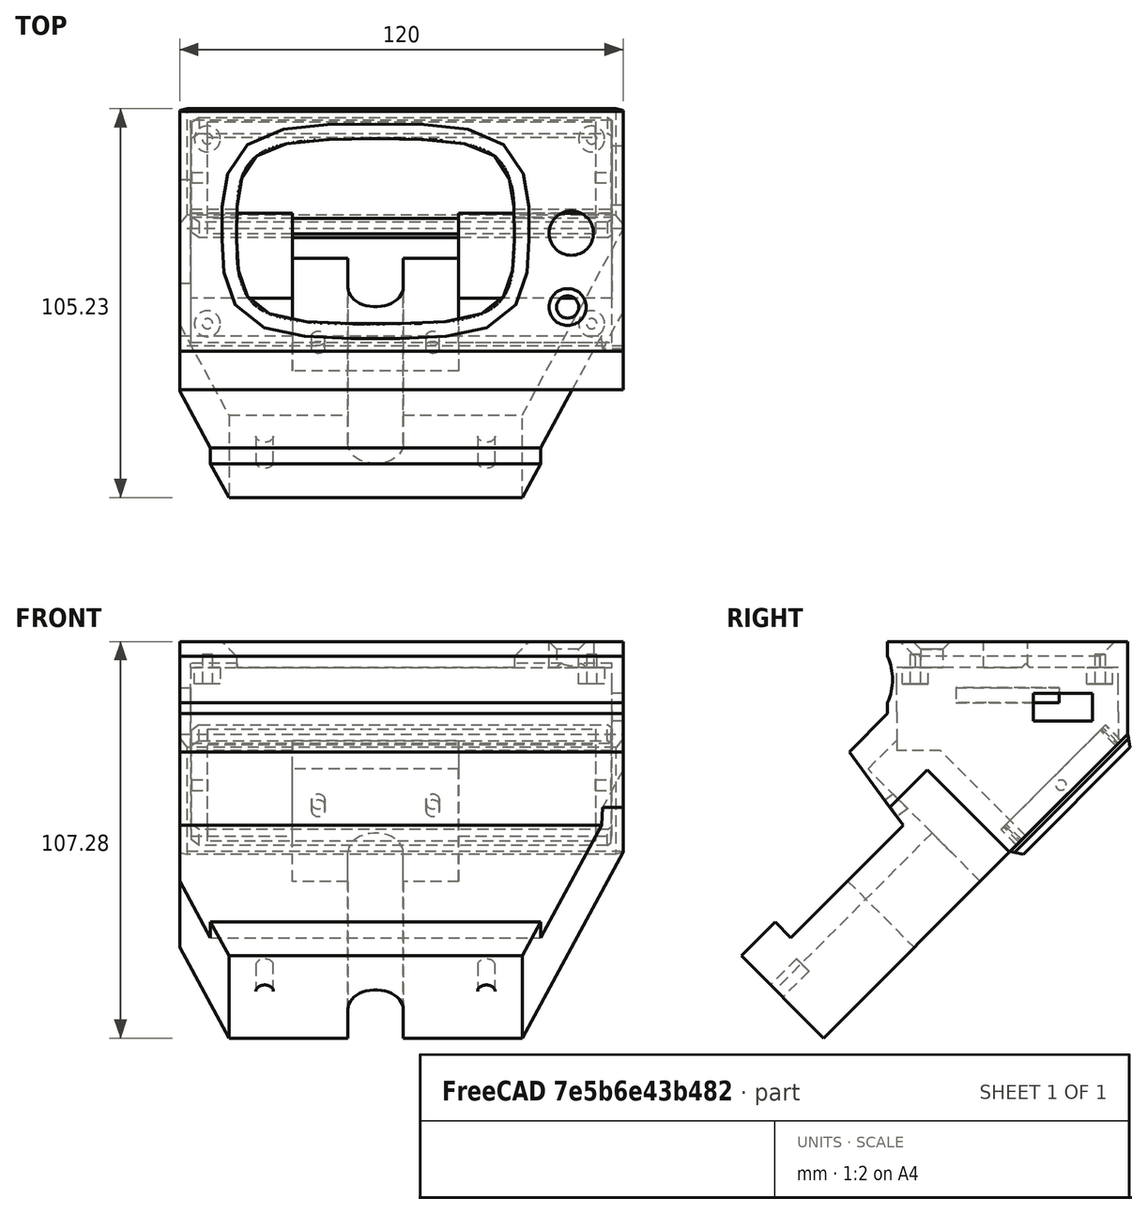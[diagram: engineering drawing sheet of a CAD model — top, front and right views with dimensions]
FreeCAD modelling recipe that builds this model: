
FCSTD DOCUMENT  (FreeCAD 0.19R)
Label: ScreenBezel2
License: All rights reserved
LicenseURL: http://en.wikipedia.org/wiki/All_rights_reserved
objects: Sketcher::SketchObject×24, PartDesign::Pocket×19, PartDesign::Chamfer×7, PartDesign::Pad×5, PartDesign::Body×2, PartDesign::Mirrored×1, Mesh::Feature×1
note: 89 computed .brp shape members not serialized (recipe doc carries the construction recipe); baked Part::Feature solids carry a one-line shape summary decoded from their .brp

FEATURE [Sketcher::SketchObject] Sketch
  FullyConstrained = true
  MapMode = 5
  Support = -> [XY_Plane]
  sketch-geometry (30):
    g0: LineSegment StartX=-53 StartY=32.5 StartZ=0 EndX=67 EndY=32.5 EndZ=0
    g1: LineSegment StartX=67 StartY=32.5 StartZ=0 EndX=67 EndY=-32.5 EndZ=0
    g2: LineSegment StartX=67 StartY=-32.5 StartZ=0 EndX=-53 EndY=-32.5 EndZ=0
    g3: LineSegment StartX=-53 StartY=-32.5 StartZ=0 EndX=-53 EndY=32.5 EndZ=0
    g4: LineSegment StartX=-37 StartY=24.5 StartZ=0 EndX=37 EndY=24.5 EndZ=0
    g5: LineSegment StartX=37 StartY=24.5 StartZ=0 EndX=37 EndY=-24.5 EndZ=0
    g6: LineSegment StartX=37 StartY=-24.5 StartZ=0 EndX=-37 EndY=-24.5 EndZ=0
    g7: LineSegment StartX=-37 StartY=-24.5 StartZ=0 EndX=-37 EndY=24.5 EndZ=0
    g8: LineSegment StartX=-37.7408 StartY=25.116 StartZ=0 EndX=37.7408 EndY=25.116 EndZ=0
    g9: LineSegment StartX=37.7408 StartY=25.116 StartZ=0 EndX=37.7408 EndY=-25.116 EndZ=0
    g10: LineSegment StartX=37.7408 StartY=-25.116 StartZ=0 EndX=-37.7408 EndY=-25.116 EndZ=0
    g11: LineSegment StartX=-37.7408 StartY=-25.116 StartZ=0 EndX=-37.7408 EndY=25.116 EndZ=0
    g12-g19: Circle x8 (B-spline internal-alignment scaffolding for g20; pole/knot coordinates omitted)
    g20: BSplineCurve PolesCount=8 KnotsCount=9 Degree=3 IsPeriodic=1
    g21-g29: GeomPoint x9 (B-spline internal-alignment scaffolding for g20; pole/knot coordinates omitted)
  constraints (53):
    c: Coincident(g0,g1)
    c: Coincident(g1,g2)
    c: Coincident(g2,g3)
    c: Coincident(g3,g0)
    c: Horizontal(g0)
    c: Horizontal(g2)
    c: Vertical(g1)
    c: Vertical(g3)
    c: Coincident(g4,g5)
    c: Coincident(g5,g6)
    c: Coincident(g6,g7)
    c: Coincident(g7,g4)
    c: Horizontal(g4)
    c: Vertical(g7)
    c: Distance(g5) = 49
    c: Distance(g4,g3) = 16
    c: Distance(g0,g5) = 30
    c: Distance(g6,g2) = 8
    c: Distance(g4,g0) = 8
    c: Distance(g6) = 74
    c: Symmetric(g5,g6,g-2)
    c: Symmetric(g5,g4,g-1)
    c: Coincident(g8,g9)
    c: Coincident(g9,g10)
    c: Coincident(g10,g11)
    c: Coincident(g11,g8)
    c: Horizontal(g8)
    c: Horizontal(g10)
    c: Vertical(g9)
    c: Vertical(g11)
    c: Symmetric(g9,g8,g-1)
    c: Weight(g12) = 1
    c: Equal(g12,g13)
    c: Equal(g12,g14)
    c: Equal(g12,g15)
    c: PointOnObject(g15,g-1)
    c: Equal(g12,g16)
    c: Equal(g12,g17)
    c: PointOnObject(g17,g-2)
    c: Equal(g12,g18)
    c: Equal(g12,g19)
    c: InternalAlignment(g12-g19 -> g20) x8
    c: InternalAlignment(g21-g29 -> g20) x9
    c: Coincident(g8,g12)
    c: Coincident(g14,g8)
    c: Coincident(g16,g10)
    c: Coincident(g18,g9)
    c: Distance(g19,g5) = 0.5
    c: Symmetric(g19,g15,g-2)
    c: Distance(g17,g6) = 0.5
    c: Symmetric(g17,g13,g-1)
    c: DistanceX(g8) = 37.7408
    c: DistanceY(g8) = 25.116
FEATURE [PartDesign::Pad] Pad
  Direction = (1,1,1)
  Length = 25
  Length2 = 100
  Profile = -> Sketch
  Type = 0
FEATURE [Sketcher::SketchObject] Sketch004  label="knob"
  FullyConstrained = false
  MapMode = 5
  Placement = pos=(0,0,0) rot=(1,0,0;3.14159rad)
  sketch-geometry (1):
    g0: Circle CenterX=52 CenterY=20.5 CenterZ=0 NormalX=0 NormalY=0 NormalZ=1 AngleXU=0 Radius=3
  constraints (1):
    c: Diameter(g0) = 6
FEATURE [PartDesign::Pocket] Pocket001
  BaseFeature = -> Pad
  Length = 5
  Length2 = 100
  Profile = -> Sketch004
  Type = 1
FEATURE [Sketcher::SketchObject] Sketch001  label="knob001"
  FullyConstrained = false
  MapMode = 5
  Placement = pos=(0,0,25) rot=(0,0,1;0rad)
  Support = -> [Pocket001]
  sketch-geometry (1):
    g0: Circle CenterX=53 CenterY=-0.5 CenterZ=0 NormalX=0 NormalY=0 NormalZ=1 AngleXU=0 Radius=6
  constraints (2):
    c: Diameter(g0) = 12
    c: DistanceY(g0) = -0.5
FEATURE [PartDesign::Pocket] Pocket
  BaseFeature = -> Pocket001
  Length = 5
  Length2 = 100
  Profile = -> Sketch001
  Type = 1
FEATURE [Sketcher::SketchObject] Sketch005  label="MainPCBPocket"
  FullyConstrained = true
  MapMode = 5
  Placement = pos=(0,0,0) rot=(1,0,0;3.14159rad)
  Support = -> [Pocket]
  sketch-geometry (4):
    g0: LineSegment StartX=-50 StartY=30 StartZ=0 EndX=64 EndY=30 EndZ=0
    g1: LineSegment StartX=64 StartY=30 StartZ=0 EndX=64 EndY=-30 EndZ=0
    g2: LineSegment StartX=64 StartY=-30 StartZ=0 EndX=-50 EndY=-30 EndZ=0
    g3: LineSegment StartX=-50 StartY=-30 StartZ=0 EndX=-50 EndY=30 EndZ=0
  constraints (11):
    c: Coincident(g0,g1)
    c: Coincident(g1,g2)
    c: Coincident(g2,g3)
    c: Coincident(g3,g0)
    c: Horizontal(g0)
    c: Horizontal(g2)
    c: Vertical(g1)
    c: Symmetric(g2,g0,g-1)
    c: DistanceX(g0) = -50
    c: DistanceY(g0) = 30
    c: DistanceX(g1) = 64
FEATURE [PartDesign::Pocket] Pocket002
  BaseFeature = -> Pocket
  Length = 18
  Length2 = 100
  Profile = -> Sketch005
  Type = 0
FEATURE [PartDesign::Chamfer] Chamfer
  Angle = 45
  Base = -> Pocket002 [Edge19]
  BaseFeature = -> Pocket002
  ChamferType = 0
  FlipDirection = false
  Size = 4
  Size2 = 1
  SupportTransform = false
FEATURE [Sketcher::SketchObject] Sketch006  label="standofs"
  FullyConstrained = true
  MapMode = 5
  Placement = pos=(0,0,18) rot=(1,0,0;3.14159rad)
  Support = -> [Chamfer]
  sketch-geometry (4):
    g0: Circle CenterX=-45.5 CenterY=25 CenterZ=0 NormalX=0 NormalY=0 NormalZ=1 AngleXU=0 Radius=3.5
    g1: Circle CenterX=-45.5 CenterY=-25 CenterZ=0 NormalX=0 NormalY=0 NormalZ=1 AngleXU=0 Radius=3.5
    g2: Circle CenterX=58.5 CenterY=-25 CenterZ=0 NormalX=0 NormalY=0 NormalZ=1 AngleXU=0 Radius=3.5
    g3: Circle CenterX=58.5 CenterY=25 CenterZ=0 NormalX=0 NormalY=0 NormalZ=1 AngleXU=0 Radius=3.5
  constraints (10):
    c: Diameter(g0) = 7
    c: Equal(g0,g1)
    c: Equal(g0,g3)
    c: Equal(g0,g2)
    c: Symmetric(g1,g0,g-1)
    c: Symmetric(g2,g3,g-1)
    c: Distance(g3,g2) = 50
    c: Distance(g1,g0) = 50
    c: Distance(g3,g0) = 104
    c: DistanceX(g0) = -45.5
FEATURE [PartDesign::Pad] Pad001
  BaseFeature = -> Chamfer
  Direction = (1,1,1)
  Length = 4.5
  Length2 = 100
  Profile = -> Sketch006
  Type = 0
FEATURE [Sketcher::SketchObject] Sketch007  label="holes"
  FullyConstrained = true
  MapMode = 5
  Placement = pos=(0,0,13.5) rot=(1,0,0;3.14159rad)
  Support = -> [Pad001]
  sketch-geometry (4):
    g0: Circle CenterX=-45.5 CenterY=25 CenterZ=0 NormalX=0 NormalY=0 NormalZ=1 AngleXU=0 Radius=1.4
    g1: Circle CenterX=58.5 CenterY=25 CenterZ=0 NormalX=0 NormalY=0 NormalZ=1 AngleXU=0 Radius=1.4
    g2: Circle CenterX=58.5 CenterY=-25 CenterZ=0 NormalX=0 NormalY=0 NormalZ=1 AngleXU=0 Radius=1.4
    g3: Circle CenterX=-45.5 CenterY=-25 CenterZ=0 NormalX=0 NormalY=0 NormalZ=1 AngleXU=0 Radius=1.4
  constraints (10):
    c: Distance(g3,g2) = 104
    c: Distance(g3,g0) = 50
    c: Symmetric(g3,g0,g-1)
    c: Symmetric(g2,g1,g-1)
    c: Diameter(g1) = 2.8
    c: Equal(g1,g2)
    c: Equal(g1,g3)
    c: Equal(g1,g0)
    c: DistanceX(g0) = -45.5
    c: Distance(g1,g2) = 50
FEATURE [PartDesign::Pocket] Pocket003
  BaseFeature = -> Pad001
  Length = 8
  Length2 = 100
  Profile = -> Sketch007
  Type = 0
FEATURE [Sketcher::SketchObject] Sketch008  label="USBhole"
  ExternalGeometry = -> [Pocket003]
  FullyConstrained = true
  MapMode = 5
  Placement = pos=(67,0,0) rot=(0.57735,0.57735,0.57735;2.0944rad)
  Support = -> [Pocket003]
  sketch-geometry (4):
    g0: LineSegment StartX=7 StartY=6.5 StartZ=0 EndX=23 EndY=6.5 EndZ=0
    g1: LineSegment StartX=23 StartY=6.5 StartZ=0 EndX=23 EndY=0 EndZ=0
    g2: LineSegment StartX=23 StartY=0 StartZ=0 EndX=7 EndY=0 EndZ=0
    g3: LineSegment StartX=7 StartY=0 StartZ=0 EndX=7 EndY=6.5 EndZ=0
  constraints (12):
    c: Coincident(g0,g1)
    c: Coincident(g1,g2)
    c: Coincident(g2,g3)
    c: Coincident(g3,g0)
    c: Horizontal(g0)
    c: Horizontal(g2)
    c: Vertical(g1)
    c: Vertical(g3)
    c: Distance(g-3,g0) = 7
    c: Distance(g0) = 16
    c: Distance(g0,g-4) = 7
    c: PointOnObject(g1,g-1)
FEATURE [PartDesign::Pocket] Pocket004
  BaseFeature = -> Pocket003
  Length = 9
  Length2 = 100
  Profile = -> Sketch008
  Type = 0
FEATURE [Sketcher::SketchObject] Sketch009  label="SDHole"
  ExternalGeometry = -> [Pocket004]
  FullyConstrained = true
  MapMode = 5
  Placement = pos=(-53,0,0) rot=(0.57735,-0.57735,-0.57735;2.0944rad)
  Support = -> [Pocket004]
  sketch-geometry (4):
    g0: LineSegment StartX=-14 StartY=12.5 StartZ=0 EndX=14 EndY=12.5 EndZ=0
    g1: LineSegment StartX=14 StartY=12.5 StartZ=0 EndX=14 EndY=8.5 EndZ=0
    g2: LineSegment StartX=14 StartY=8.5 StartZ=0 EndX=-14 EndY=8.5 EndZ=0
    g3: LineSegment StartX=-14 StartY=8.5 StartZ=0 EndX=-14 EndY=12.5 EndZ=0
  constraints (11):
    c: Coincident(g0,g1)
    c: Coincident(g1,g2)
    c: Coincident(g2,g3)
    c: Coincident(g3,g0)
    c: Horizontal(g0)
    c: Vertical(g1)
    c: Vertical(g3)
    c: Distance(g0,g-3) = 1
    c: Distance(g1) = 4
    c: Symmetric(g1,g2,g-2)
    c: Distance(g2) = 28
FEATURE [PartDesign::Pocket] Pocket005
  BaseFeature = -> Pocket004
  Length = 5
  Length2 = 100
  Profile = -> Sketch009
  Type = 0
FEATURE [Sketcher::SketchObject] Sketch010  label="TowerProper"
  FullyConstrained = false
  MapMode = 5
  Placement = pos=(-53,0,0) rot=(0.57735,-0.57735,-0.57735;2.0944rad)
  Support = -> [Pocket005]
  sketch-geometry (6):
    g0: LineSegment StartX=-32.5 StartY=0 StartZ=0 EndX=49.783 EndY=-82.283 EndZ=0
    g1: LineSegment StartX=49.783 StartY=-82.283 StartZ=0 EndX=85.033 EndY=-47.033 EndZ=0
    g2: LineSegment StartX=85.033 StartY=-47.033 StartZ=0 EndX=32 EndY=6 EndZ=0
    g3: LineSegment StartX=-0.680195 StartY=-31.8198 StartZ=0 EndX=-60.5279 EndY=28.0279 EndZ=0
    g4: LineSegment StartX=32 StartY=6 StartZ=0 EndX=-32.5 EndY=6 EndZ=0
    g5: LineSegment StartX=-32.5 StartY=6 StartZ=0 EndX=-32.5 EndY=0 EndZ=0
  constraints (15):
    c: Coincident(g0,g1)
    c: Coincident(g1,g2)
    c: Parallel(g0,g2)
    c: Perpendicular(g0,g1)
    c: PointOnObject(g5,g-1)
    c: Coincident(g4,g2)
    c: Horizontal(g4)
    c: DistanceX(g4) = -32.5
    c: Coincident(g5,g4)
    c: Vertical(g5)
    c: DistanceY(g4) = 6
    c: DistanceX(g2) = 32
    c: Coincident(g0,g5)
    c: Angle(g0) = -0.785398
    c: Distance(g2) = 75
FEATURE [PartDesign::Pad] Pad002  label="Backbit"
  BaseFeature = -> Pocket005
  Direction = (1,1,1)
  Length = 120
  Length2 = 100
  Profile = -> Sketch010
  Reversed = true
  Type = 0
FEATURE [Sketcher::SketchObject] Sketch015  label="hollowOutPocket"
  FullyConstrained = true
  MapMode = 5
  Placement = pos=(0,0,13.5) rot=(1,0,0;3.14159rad)
  sketch-geometry (4):
    g0: LineSegment StartX=-50 StartY=30 StartZ=0 EndX=64 EndY=30 EndZ=0
    g1: LineSegment StartX=64 StartY=30 StartZ=0 EndX=64 EndY=-30 EndZ=0
    g2: LineSegment StartX=64 StartY=-30 StartZ=0 EndX=-50 EndY=-30 EndZ=0
    g3: LineSegment StartX=-50 StartY=-30 StartZ=0 EndX=-50 EndY=30 EndZ=0
  constraints (11):
    c: Coincident(g0,g1)
    c: Coincident(g1,g2)
    c: Coincident(g2,g3)
    c: Coincident(g3,g0)
    c: Horizontal(g0)
    c: Horizontal(g2)
    c: Vertical(g1)
    c: DistanceX(g0) = 64
    c: DistanceX(g0) = -50
    c: Distance(g3) = 60
    c: Symmetric(g2,g0,g-1)
FEATURE [PartDesign::Pocket] Pocket006
  BaseFeature = -> Pad002
  Length = 18
  Length2 = 100
  Profile = -> Sketch015
  Reversed = true
  Type = 0
FEATURE [Sketcher::SketchObject] Sketch016  label="UsbRetrim"
  FullyConstrained = true
  MapMode = 5
  Placement = pos=(67,0,0) rot=(0.57735,0.57735,0.57735;2.0944rad)
  Support = -> [Pocket006]
  sketch-geometry (4):
    g0: LineSegment StartX=7 StartY=11 StartZ=0 EndX=23 EndY=11 EndZ=0
    g1: LineSegment StartX=23 StartY=11 StartZ=0 EndX=23 EndY=3.5 EndZ=0
    g2: LineSegment StartX=23 StartY=3.5 StartZ=0 EndX=7 EndY=3.5 EndZ=0
    g3: LineSegment StartX=7 StartY=3.5 StartZ=0 EndX=7 EndY=11 EndZ=0
  constraints (12):
    c: Coincident(g0,g1)
    c: Coincident(g1,g2)
    c: Coincident(g2,g3)
    c: Coincident(g3,g0)
    c: Horizontal(g0)
    c: Horizontal(g2)
    c: Vertical(g1)
    c: Vertical(g3)
    c: Distance(g1) = 7.5
    c: Distance(g2) = 16
    c: DistanceX(g0) = 7
    c: DistanceY(g0) = 11
FEATURE [PartDesign::Pocket] Pocket007
  BaseFeature = -> Pocket006
  Length = 9
  Length2 = 100
  Profile = -> Sketch016
  Type = 0
FEATURE [PartDesign::Chamfer] Chamfer001
  Angle = 45
  Base = -> Pocket007 [Edge6]
  BaseFeature = -> Pocket007
  ChamferType = 0
  FlipDirection = false
  Size = 2
  Size2 = 1
  SupportTransform = false
FEATURE [Sketcher::SketchObject] Sketch018
  FullyConstrained = true
  MapMode = 5
  Placement = pos=(0,0,0) rot=(1,0,0;1.5708rad)
  Support = -> [XZ_Plane001]
  sketch-geometry (4):
    g0: LineSegment StartX=-60 StartY=22.5 StartZ=0 EndX=60 EndY=22.5 EndZ=0
    g1: LineSegment StartX=60 StartY=22.5 StartZ=0 EndX=60 EndY=-22.5 EndZ=0
    g2: LineSegment StartX=60 StartY=-22.5 StartZ=0 EndX=-60 EndY=-22.5 EndZ=0
    g3: LineSegment StartX=-60 StartY=-22.5 StartZ=0 EndX=-60 EndY=22.5 EndZ=0
  constraints (10):
    c: Coincident(g0,g1)
    c: Coincident(g1,g2)
    c: Coincident(g2,g3)
    c: Coincident(g3,g0)
    c: Horizontal(g2)
    c: Vertical(g3)
    c: Symmetric(g0,g0,g-2)
    c: Distance(g0) = 120
    c: Distance(g1) = 45
    c: Symmetric(g1,g0,g-1)
FEATURE [PartDesign::Pad] Pad003
  Direction = (1,1,1)
  Length = 3
  Length2 = 100
  Placement = pos=(0,0,0) rot=(1,0,0;1.5708rad)
  Profile = -> Sketch018
  Type = 0
FEATURE [Sketcher::SketchObject] Sketch019
  FullyConstrained = true
  MapMode = 5
  Placement = pos=(0,-3,7e-16) rot=(1,0,0;1.5708rad)
  Support = -> [Pad003]
  sketch-geometry (4):
    g0: LineSegment StartX=-56.75 StartY=20 StartZ=0 EndX=56.75 EndY=20 EndZ=0
    g1: LineSegment StartX=56.75 StartY=20 StartZ=0 EndX=56.75 EndY=-20 EndZ=0
    g2: LineSegment StartX=56.75 StartY=-20 StartZ=0 EndX=-56.75 EndY=-20 EndZ=0
    g3: LineSegment StartX=-56.75 StartY=-20 StartZ=0 EndX=-56.75 EndY=20 EndZ=0
  constraints (11):
    c: Coincident(g0,g1)
    c: Coincident(g1,g2)
    c: Coincident(g2,g3)
    c: Coincident(g3,g0)
    c: Horizontal(g0)
    c: Horizontal(g2)
    c: Vertical(g1)
    c: Vertical(g3)
    c: Distance(g0) = 113.5
    c: Distance(g1) = 40
    c: Symmetric(g1,g0,g-1)
FEATURE [PartDesign::Pad] Pad004
  BaseFeature = -> Pad003
  Direction = (1,1,1)
  Length = 6
  Length2 = 100
  Placement = pos=(0,0,0) rot=(1,0,0;1.5708rad)
  Profile = -> Sketch019
  Type = 0
FEATURE [Sketcher::SketchObject] Sketch020
  FullyConstrained = true
  MapMode = 5
  Placement = pos=(56.75,0,0) rot=(0.707107,0,0.707107;3.14159rad)
  Support = -> [Pad004]
  sketch-geometry (1):
    g0: Circle CenterX=0 CenterY=6 CenterZ=0 NormalX=0 NormalY=0 NormalZ=1 AngleXU=0 Radius=1.4
  constraints (3):
    c: PointOnObject(g0,g-2)
    c: Diameter(g0) = 2.8
    c: DistanceY(g0) = 6
FEATURE [PartDesign::Pocket] Pocket008
  BaseFeature = -> Pad004
  Length = 5
  Length2 = 100
  Placement = pos=(0,0,0) rot=(1,0,0;1.5708rad)
  Profile = -> Sketch020
  Type = 1
FEATURE [Sketcher::SketchObject] Sketch021
  FullyConstrained = true
  MapMode = 5
  Placement = pos=(0,-9,1.5e-14) rot=(1,0,0;1.5708rad)
  sketch-geometry (4):
    g0: LineSegment StartX=-52.5 StartY=18.5 StartZ=0 EndX=52.5 EndY=18.5 EndZ=0
    g1: LineSegment StartX=52.5 StartY=18.5 StartZ=0 EndX=52.5 EndY=-18.5 EndZ=0
    g2: LineSegment StartX=52.5 StartY=-18.5 StartZ=0 EndX=-52.5 EndY=-18.5 EndZ=0
    g3: LineSegment StartX=-52.5 StartY=-18.5 StartZ=0 EndX=-52.5 EndY=18.5 EndZ=0
  constraints (11):
    c: Coincident(g0,g1)
    c: Coincident(g1,g2)
    c: Coincident(g2,g3)
    c: Coincident(g3,g0)
    c: Horizontal(g0)
    c: Horizontal(g2)
    c: Vertical(g1)
    c: Vertical(g3)
    c: Distance(g0) = 105
    c: Symmetric(g0,g2,g-1)
    c: Distance(g1) = 37
FEATURE [Sketcher::SketchObject] Sketch024
  ExternalGeometry = -> [Pocket008]
  FullyConstrained = false
  MapMode = 5
  Placement = pos=(60,0,0) rot=(0.707107,0,0.707107;3.14159rad)
  Support = -> [Pocket008]
  sketch-geometry (3):
    g0: LineSegment StartX=-22.5 StartY=3 StartZ=0 EndX=-17.8755 EndY=-3.60453 EndZ=0
    g1: LineSegment StartX=-17.8755 StartY=-3.60453 StartZ=0 EndX=-35.5163 EndY=-3.60453 EndZ=0
    g2: LineSegment StartX=-35.5163 StartY=-3.60453 StartZ=0 EndX=-22.5 EndY=3 EndZ=0
  constraints (6):
    c: Coincident(g0,g1)
    c: Horizontal(g1)
    c: Coincident(g1,g2)
    c: Coincident(g2,g0)
    c: Angle(g0) = -0.959931
    c: Coincident(g0,g-3)
FEATURE [PartDesign::Pocket] Pocket012
  BaseFeature = -> Pocket008
  Length = 5
  Length2 = 100
  Placement = pos=(0,0,0) rot=(1,0,0;1.5708rad)
  Profile = -> Sketch024
  Type = 1
FEATURE [PartDesign::Mirrored] Mirrored
  BaseFeature = -> Pocket012
  MirrorPlane = -> Sketch024 [V_Axis]
  Originals = -> [Pocket012]
  Placement = pos=(0,0,0) rot=(1,0,0;1.5708rad)
FEATURE [PartDesign::Chamfer] Chamfer008
  Angle = 45
  Base = -> Mirrored [Edge14,Edge12]
  BaseFeature = -> Mirrored
  ChamferType = 0
  FlipDirection = false
  Placement = pos=(0,0,0) rot=(1,0,0;1.5708rad)
  Size = 2
  Size2 = 1
  SupportTransform = false
FEATURE [PartDesign::Pocket] Pocket013
  BaseFeature = -> Chamfer008
  Length = 6
  Length2 = 100
  Placement = pos=(0,0,0) rot=(1,0,0;1.5708rad)
  Profile = -> Sketch021
  Type = 0
FEATURE [PartDesign::Chamfer] Chamfer009
  Angle = 45
  Base = -> Pocket013 [Edge29]
  BaseFeature = -> Pocket013
  ChamferType = 0
  FlipDirection = false
  Placement = pos=(0,0,0) rot=(1,0,0;1.5708rad)
  Size = 2
  Size2 = 1
  SupportTransform = false
FEATURE [PartDesign::Chamfer] Chamfer010
  Angle = 45
  Base = -> Chamfer009 [Edge11]
  BaseFeature = -> Chamfer009
  ChamferType = 0
  FlipDirection = false
  Placement = pos=(0,0,0) rot=(1,0,0;1.5708rad)
  Size = 1
  Size2 = 1
  SupportTransform = false
FEATURE [PartDesign::Chamfer] Chamfer011
  Angle = 45
  Base = -> Chamfer010 [Edge18]
  BaseFeature = -> Chamfer010
  ChamferType = 0
  FlipDirection = false
  Placement = pos=(0,0,0) rot=(1,0,0;1.5708rad)
  Size = 1
  Size2 = 1
  SupportTransform = false
FEATURE [PartDesign::Chamfer] Chamfer012
  Angle = 45
  Base = -> Chamfer011 [Edge20]
  BaseFeature = -> Chamfer011
  ChamferType = 0
  FlipDirection = false
  Placement = pos=(0,0,0) rot=(1,0,0;1.5708rad)
  Size = 2
  Size2 = 1
  SupportTransform = false
FEATURE [PartDesign::Body] Body001  label="BoxCap"
  Group = -> [Sketch018,Pad003,Sketch019,Pad004,Sketch020,Pocket008,Sketch021,Sketch024,Pocket012,Mirrored,Chamfer008,Pocket013,Chamfer009,Chamfer010,Chamfer011,Chamfer012]
  Origin = -> Origin001
  Placement = pos=(7,18.751,-18.0573) rot=(-1,0,0;0.785398rad)
  Tip = -> Chamfer012
FEATURE [Sketcher::SketchObject] Sketch033  label="beltPath"
  FullyConstrained = false
  MapMode = 5
  Placement = pos=(-53,0,0) rot=(0.57735,-0.57735,-0.57735;2.0944rad)
  sketch-geometry (6):
    g0: LineSegment StartX=72.0852 StartY=-60.0601 StartZ=0 EndX=62.8928 EndY=-50.8678 EndZ=0
    g1: LineSegment StartX=62.8928 StartY=-50.8678 StartZ=0 EndX=58.6502 EndY=-55.1104 EndZ=0
    g2: LineSegment StartX=58.6502 StartY=-55.1104 StartZ=0 EndX=28.2446 EndY=-24.7048 EndZ=0
    g3: LineSegment StartX=28.2446 StartY=-24.7048 StartZ=0 EndX=69.9604 EndY=32.2098 EndZ=0
    g4: LineSegment StartX=69.9604 StartY=32.2098 StartZ=0 EndX=106.753 EndY=-43.13 EndZ=0
    g5: LineSegment StartX=72.0852 StartY=-60.0601 StartZ=0 EndX=106.753 EndY=-43.13 EndZ=0
  constraints (13):
    c: Coincident(g1,g0)
    c: Coincident(g2,g1)
    c: Coincident(g3,g2)
    c: Coincident(g4,g3)
    c: Coincident(g5,g0)
    c: Coincident(g5,g4)
    c: Perpendicular(g4,g5)
    c: Distance(g0) = 13
    c: Angle(g2) = 2.35619
    c: Angle(g1) = -2.35619
    c: Angle(g0) = 2.35619
    c: Distance(g1) = 6
    c: Distance(g2) = 43
FEATURE [Sketcher::SketchObject] Sketch036  label="Stepper3mm"
  FullyConstrained = false
  MapMode = 5
  Placement = pos=(0,-29.9249,-22.0846) rot=(1,0,0;2.20657rad)
  sketch-geometry (21):
    g0: ArcOfCircle CenterX=15.5 CenterY=3.5 CenterZ=0 NormalX=0 NormalY=0 NormalZ=1 AngleXU=0 Radius=1.75 StartAngle=9e-16 EndAngle=3.14159
    g1: ArcOfCircle CenterX=15.5 CenterY=1.5 CenterZ=0 NormalX=0 NormalY=0 NormalZ=1 AngleXU=0 Radius=1.75 StartAngle=3.14159 EndAngle=6.28319
    g2: LineSegment StartX=13.75 StartY=3.5 StartZ=0 EndX=13.75 EndY=1.5 EndZ=0
    g3: LineSegment StartX=17.25 StartY=3.5 StartZ=0 EndX=17.25 EndY=1.5 EndZ=0
    g4: ArcOfCircle CenterX=-15.5 CenterY=3.5 CenterZ=0 NormalX=0 NormalY=0 NormalZ=1 AngleXU=0 Radius=1.75 StartAngle=1e-16 EndAngle=3.14159
    g5: ArcOfCircle CenterX=-15.5 CenterY=1.5 CenterZ=0 NormalX=0 NormalY=0 NormalZ=1 AngleXU=0 Radius=1.75 StartAngle=3.14159 EndAngle=6.28319
    g6: LineSegment StartX=-17.25 StartY=3.5 StartZ=0 EndX=-17.25 EndY=1.5 EndZ=0
    g7: LineSegment StartX=-13.75 StartY=3.5 StartZ=0 EndX=-13.75 EndY=1.5 EndZ=0
    g8: ArcOfCircle CenterX=-15.5 CenterY=-27.5 CenterZ=0 NormalX=0 NormalY=0 NormalZ=1 AngleXU=0 Radius=1.75 StartAngle=0 EndAngle=3.14159
    g9: ArcOfCircle CenterX=-15.5 CenterY=-29.5 CenterZ=0 NormalX=0 NormalY=0 NormalZ=1 AngleXU=0 Radius=1.75 StartAngle=3.14159 EndAngle=6.28319
    g10: LineSegment StartX=-17.25 StartY=-27.5 StartZ=0 EndX=-17.25 EndY=-29.5 EndZ=0
    g11: LineSegment StartX=-13.75 StartY=-27.5 StartZ=0 EndX=-13.75 EndY=-29.5 EndZ=0
    g12: ArcOfCircle CenterX=15.5 CenterY=-27.5 CenterZ=0 NormalX=0 NormalY=0 NormalZ=1 AngleXU=0 Radius=1.75 StartAngle=3e-16 EndAngle=3.14159
    g13: ArcOfCircle CenterX=15.5 CenterY=-29.5 CenterZ=0 NormalX=0 NormalY=0 NormalZ=1 AngleXU=0 Radius=1.75 StartAngle=3.14159 EndAngle=6.28319
    g14: LineSegment StartX=13.75 StartY=-27.5 StartZ=0 EndX=13.75 EndY=-29.5 EndZ=0
    g15: LineSegment StartX=17.25 StartY=-27.5 StartZ=0 EndX=17.25 EndY=-29.5 EndZ=0
    g16: LineSegment StartX=-15.5 StartY=3.5 StartZ=0 EndX=15.5 EndY=3.5 EndZ=0
    g17: LineSegment StartX=15.5 StartY=3.5 StartZ=0 EndX=15.5 EndY=-27.5 EndZ=0
    g18: LineSegment StartX=15.5 StartY=-27.5 StartZ=0 EndX=-15.5 EndY=-27.5 EndZ=0
    g19: LineSegment StartX=-15.5 StartY=-27.5 StartZ=0 EndX=-15.5 EndY=3.5 EndZ=0
    g20: Circle CenterX=-2e-16 CenterY=-12 CenterZ=0 NormalX=0 NormalY=0 NormalZ=1 AngleXU=0 Radius=3.20765
  constraints (48):
    c: Tangent(g0,g3) = 1.5708
    c: Tangent(g0,g2) = -1.5708
    c: Tangent(g2,g1) = -1.5708
    c: Tangent(g3,g1) = 1.5708
    c: Vertical(g2)
    c: Equal(g0,g1)
    c: Tangent(g4,g7) = 1.5708
    c: Tangent(g4,g6) = -1.5708
    c: Tangent(g6,g5) = -1.5708
    c: Tangent(g7,g5) = 1.5708
    c: Vertical(g6)
    c: Equal(g4,g5)
    c: Tangent(g8,g11) = 1.5708
    c: Tangent(g8,g10) = -1.5708
    c: Tangent(g10,g9) = -1.5708
    c: Tangent(g11,g9) = 1.5708
    c: Vertical(g10)
    c: Equal(g8,g9)
    c: Tangent(g12,g15) = 1.5708
    c: Tangent(g12,g14) = -1.5708
    c: Tangent(g14,g13) = -1.5708
    c: Tangent(g15,g13) = 1.5708
    c: Vertical(g14)
    c: Equal(g12,g13)
    c: Coincident(g16,g4)
    c: Coincident(g16,g0)
    c: Coincident(g16,g17)
    c: Coincident(g17,g12)
    c: Coincident(g17,g18)
    c: Coincident(g18,g8)
    c: Coincident(g18,g19)
    c: Coincident(g19,g16)
    c: Equal(g19,g16)
    c: Equal(g16,g18)
    c: Equal(g18,g17)
    c: Diameter(g4) = 3.5
    c: Equal(g4,g0)
    c: Equal(g4,g12)
    c: Equal(g4,g8)
    c: Equal(g7,g3)
    c: Equal(g3,g15)
    c: Equal(g15,g11)
    c: Distance(g7) = 2
    c: Distance(g17) = 31
    c: Symmetric(g0,g4,g-2)
    c: Symmetric(g0,g8,g20)
    c: Vertical(g17)
    c: DistanceY(g20) = -12
FEATURE [Sketcher::SketchObject] Sketch041  label="ScreenBack"
  FullyConstrained = false
  MapMode = 5
  Placement = pos=(0,16.25,-16.25) rot=(1,0,0;3.92699rad)
  Support = -> [Pocket006]
  sketch-geometry (4):
    g0: LineSegment StartX=-50 StartY=16 StartZ=0 EndX=64 EndY=16 EndZ=0
    g1: LineSegment StartX=64 StartY=16 StartZ=0 EndX=64 EndY=-16.9876 EndZ=0
    g2: LineSegment StartX=64 StartY=-16.9876 StartZ=0 EndX=-50 EndY=-16.9876 EndZ=0
    g3: LineSegment StartX=-50 StartY=-16.9876 StartZ=0 EndX=-50 EndY=16 EndZ=0
  constraints (11):
    c: Coincident(g0,g1)
    c: Coincident(g1,g2)
    c: Coincident(g2,g3)
    c: Coincident(g3,g0)
    c: Horizontal(g0)
    c: Horizontal(g2)
    c: Vertical(g1)
    c: Vertical(g3)
    c: DistanceX(g0) = -50
    c: DistanceX(g0) = 64
    c: DistanceY(g0) = 16
FEATURE [PartDesign::Pocket] Pocket019
  BaseFeature = -> Chamfer001
  Length = 33
  Length2 = 100
  Profile = -> Sketch041
  Type = 0
FEATURE [Sketcher::SketchObject] Sketch031  label="StepperSlot17"
  ExternalGeometry = -> [Chamfer001]
  FullyConstrained = false
  MapMode = 5
  Placement = pos=(0,16.25,-16.25) rot=(1,0,0;3.92699rad)
  Support = -> [Pocket019]
  sketch-geometry (4):
    g0: LineSegment StartX=-22.5 StartY=-18.4454 StartZ=0 EndX=22.5 EndY=-18.4454 EndZ=0
    g1: LineSegment StartX=22.5 StartY=-18.4454 StartZ=0 EndX=22.5 EndY=33.3848 EndZ=0
    g2: LineSegment StartX=22.5 StartY=33.3848 StartZ=0 EndX=-22.5 EndY=33.3848 EndZ=0
    g3: LineSegment StartX=-22.5 StartY=33.3848 StartZ=0 EndX=-22.5 EndY=-18.4454 EndZ=0
  constraints (10):
    c: Coincident(g0,g1)
    c: Coincident(g1,g2)
    c: Coincident(g2,g3)
    c: Coincident(g3,g0)
    c: Horizontal(g0)
    c: Vertical(g1)
    c: Vertical(g3)
    c: Symmetric(g1,g2,g-2)
    c: Distance(g2) = 45
    c: Distance(g1,g-3) = 60
FEATURE [PartDesign::Pocket] Pocket020
  BaseFeature = -> Pocket019
  Length = 43
  Length2 = 100
  Profile = -> Sketch031
  Type = 0
FEATURE [PartDesign::Pocket] Pocket021
  BaseFeature = -> Pocket020
  Length = 5
  Length2 = 100
  Profile = -> Sketch033
  Type = 1
FEATURE [Sketcher::SketchObject] Sketch034  label="screwslot"
  FullyConstrained = false
  MapMode = 5
  Placement = pos=(0,-66.033,-66.033) rot=(1,0,0;2.35619rad)
  Support = -> [Pocket021]
  sketch-geometry (7):
    g0: ArcOfCircle CenterX=-2e-16 CenterY=-12 CenterZ=0 NormalX=0 NormalY=0 NormalZ=1 AngleXU=0 Radius=7.5 StartAngle=0 EndAngle=3.14159
    g1: LineSegment StartX=7.5 StartY=-33.2436 StartZ=0 EndX=7.5 EndY=-12 EndZ=0
    g2: LineSegment StartX=-7.5 StartY=-33.2436 StartZ=0 EndX=-7.5 EndY=-12 EndZ=0
    g3: LineSegment StartX=7.5 StartY=-33.2436 StartZ=0 EndX=3.29977 EndY=-37.4439 EndZ=0
    g4: LineSegment StartX=3.29977 StartY=-37.4439 StartZ=0 EndX=-3.29977 EndY=-37.4439 EndZ=0
    g5: LineSegment StartX=-3.29977 StartY=-37.4439 StartZ=0 EndX=-7.5 EndY=-33.2436 EndZ=0
    g6: LineSegment StartX=-1.69433 StartY=-29.9439 StartZ=0 EndX=3.32824 EndY=-29.9439 EndZ=0
  constraints (16):
    c: Tangent(g1,g0) = -1.5708
    c: Tangent(g2,g0) = 1.5708
    c: Vertical(g1)
    c: Diameter(g0) = 15
    c: Coincident(g1,g3)
    c: Coincident(g3,g4)
    c: Horizontal(g4)
    c: Coincident(g4,g5)
    c: Coincident(g5,g2)
    c: Distance(g1,g2) = 15
    c: Equal(g3,g5)
    c: Angle(g3) = -2.35619
    c: Symmetric(g1,g2,g-2)
    c: Horizontal(g6)
    c: Distance(g6,g4) = 7.5
    c: DistanceY(g0) = -12
FEATURE [Sketcher::SketchObject] Sketch042  label="MountHoles"
  FullyConstrained = false
  MapMode = 5
  Placement = pos=(0,-66.033,-66.033) rot=(1,0,0;2.35619rad)
  sketch-geometry (3):
    g0: Circle CenterX=-30 CenterY=-5 CenterZ=0 NormalX=0 NormalY=0 NormalZ=1 AngleXU=0 Radius=2.35
    g1: Circle CenterX=30 CenterY=-5 CenterZ=0 NormalX=0 NormalY=0 NormalZ=1 AngleXU=0 Radius=2.35
    g2: LineSegment StartX=0 StartY=4.11612 StartZ=0 EndX=0 EndY=-8.94769 EndZ=0
  constraints (7):
    c: Distance(g0,g1) = 60
    c: DistanceY(g1) = -5
    c: DistanceY(g0) = -5
    c: Diameter(g0) = 4.7
    c: Equal(g0,g1)
    c: Symmetric(g0,g1,g2)
    c: DistanceX(g2) = 0
FEATURE [Sketcher::SketchObject] Sketch043  label="scallop"
  FullyConstrained = true
  MapMode = 5
  Placement = pos=(-53,0,0) rot=(0.57735,-0.57735,-0.57735;2.0944rad)
  sketch-geometry (1):
    g0: Circle CenterX=46.1075 CenterY=14.7465 CenterZ=0 NormalX=0 NormalY=0 NormalZ=1 AngleXU=0 Radius=15
  constraints (3):
    c: Diameter(g0) = 30
    c: DistanceX(g0) = 46.1075
    c: DistanceY(g0) = 14.7465
FEATURE [PartDesign::Pocket] Pocket022
  BaseFeature = -> Pocket021
  Length = 65
  Length2 = 100
  Profile = -> Sketch034
  Type = 0
FEATURE [PartDesign::Pocket] Pocket023
  BaseFeature = -> Pocket022
  Length = 5
  Length2 = 100
  Profile = -> Sketch036
  Type = 0
FEATURE [PartDesign::Pocket] Pocket024
  BaseFeature = -> Pocket023
  Length = 10
  Length2 = 100
  Profile = -> Sketch042
  Type = 0
FEATURE [PartDesign::Pocket] Pocket025
  BaseFeature = -> Pocket024
  Length = 5
  Length2 = 100
  Profile = -> Sketch043
  Type = 1
FEATURE [Sketcher::SketchObject] Sketch044  label="angle"
  FullyConstrained = false
  MapMode = 5
  Placement = pos=(0,-6.01253,6.01253) rot=(1,0,0;0.785398rad)
  Support = -> [Pocket025]
  sketch-geometry (7):
    g0: LineSegment StartX=75.5253 StartY=0 StartZ=0 EndX=35 EndY=-105.599 EndZ=0
    g1: LineSegment StartX=35 StartY=-105.599 StartZ=0 EndX=-35 EndY=-105.599 EndZ=0
    g2: LineSegment StartX=-35 StartY=-105.599 StartZ=0 EndX=-75.5253 EndY=0 EndZ=0
    g3: LineSegment StartX=-75.5253 StartY=0 StartZ=0 EndX=-103.489 EndY=-26.5131 EndZ=0
    g4: LineSegment StartX=-103.489 StartY=-26.5131 StartZ=0 EndX=-83.2306 EndY=-139.493 EndZ=0
    g5: LineSegment StartX=-83.2306 StartY=-139.493 StartZ=0 EndX=94.2253 EndY=-139.493 EndZ=0
    g6: LineSegment StartX=94.2253 StartY=-139.493 StartZ=0 EndX=75.5253 EndY=0 EndZ=0
  constraints (12):
    c: Coincident(g0,g1)
    c: Coincident(g1,g2)
    c: Coincident(g2,g3)
    c: Coincident(g3,g4)
    c: Coincident(g4,g5)
    c: Horizontal(g5)
    c: Coincident(g5,g6)
    c: Coincident(g6,g0)
    c: Symmetric(g0,g1,g-2)
    c: Distance(g1) = 70
    c: PointOnObject(g2,g-1)
    c: Symmetric(g0,g2,g-2)
FEATURE [PartDesign::Pocket] Pocket026
  BaseFeature = -> Pocket025
  Length = 5
  Length2 = 100
  Profile = -> Sketch044
  Type = 1
FEATURE [PartDesign::Body] Body  label="ScreenBox"
  Group = -> [Sketch,Pad,Sketch001,Sketch004,Pocket001,Pocket,Sketch005,Pocket002,Chamfer,Sketch006,Pad001,Sketch007,Pocket003,Sketch008,Pocket004,Sketch009,Pocket005,Sketch010,Pad002,Sketch015,Pocket006,Sketch016,Pocket007,Chamfer001,Sketch031,Sketch033,Sketch034,Sketch036,Sketch041,Pocket019,Pocket020,Pocket021,Sketch042,Sketch043,Sketch044,Pocket022,Pocket023,Pocket024,Pocket025,Pocket026]
  Origin = -> Origin
  Tip = -> Pocket026
FEATURE [Mesh::Feature] Mesh  label="Pocket026 (Meshed)"
